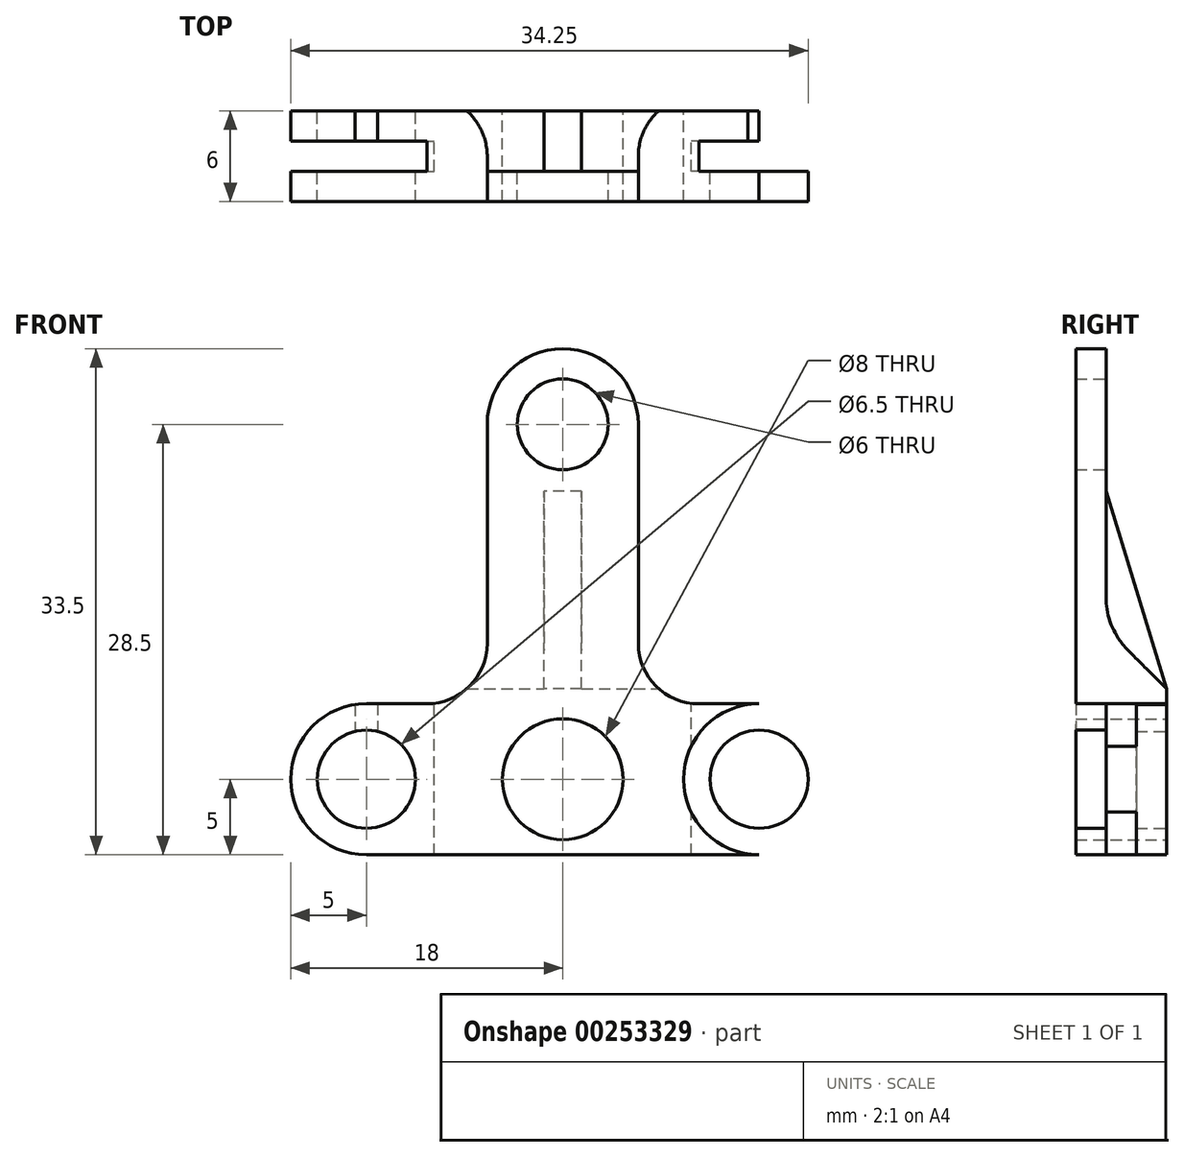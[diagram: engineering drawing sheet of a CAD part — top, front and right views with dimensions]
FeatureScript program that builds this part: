
annotation { "Feature Type Name" : "Feature", "Feature Type Description" : "" }
export const myFeature = defineFeature(function(context is Context, id is Id, definition is map)
    precondition{}
    {
        {
            var Q0;
            Q0=qCreatedBy(makeId("Front.planeOp"),FACE);
            var sketch = newSketch(context, id + "F0", { "sketchPlane" : qUnion([Q0])});
            skCircle(sketch, "E0", {"center": v(-13, 0) * mm, "radius": 3.25 * mm});
            skCircle(sketch, "E1", {"center": v(-13, 0) * mm, "radius": 5 * mm});
            skCircle(sketch, "E2", {"center": v(0, 0) * mm, "radius": 4 * mm});
            skCircle(sketch, "E3", {"center": v(0, 23.5) * mm, "radius": 3 * mm});
            skArc(sketch, "E4", {"start": v(5, 23.5) * mm, "mid": v(0, 28.5) * mm, "end": v(-5, 23.5) * mm});
            skCircle(sketch, "E5.MirrorC", {"center": v(13, 0) * mm, "radius": 5 * mm});
            skCircle(sketch, "E6.MirrorC", {"center": v(13, 0) * mm, "radius": 3.25 * mm});
            skLineSegment(sketch, "E7", {"start": v(-5, 23.5) * mm, "end": v(-5, 9) * mm});
            skLineSegment(sketch, "E8", {"start": v(-13, 5) * mm, "end": v(-9, 5) * mm});
            skArc(sketch, "E9", {"start": v(-9, 5) * mm, "mid": v(-6.17, 6.17) * mm, "end": v(-5, 9) * mm});
            skLineSegment(sketch, "E10.MirrorCS", {"start": v(5, 23.5) * mm, "end": v(5, 9) * mm});
            skArc(sketch, "E11.MirrorCS", {"start": v(9, 5) * mm, "mid": v(6.17, 6.17) * mm, "end": v(5, 9) * mm});
            skLineSegment(sketch, "E12.MirrorCS", {"start": v(13, 5) * mm, "end": v(9, 5) * mm});
            skLineSegment(sketch, "E13", {"start": v(-13, -5) * mm, "end": v(13, -5) * mm});
            skSolve(sketch);
        }
        {
            var Q0;
            Q0=makeQuery(id+"F0.imprint","IMPRINT",FACE,{"disambiguationData":[TD([[makeQuery(id+"F0.imprint","IMPRINT",EDGE,{"derivedFrom":sQuery(id+"F0.wireOp",EDGE,"E2")}),-1.0]])]});
            var Q1;
            Q1=makeQuery(id+"F0.imprint","IMPRINT",FACE,{"disambiguationData":[TD([[makeQuery(id+"F0.imprint","IMPRINT",EDGE,{"derivedFrom":sQuery(id+"F0.wireOp",EDGE,"E0")}),-1.0]])]});
            var Q2;
            Q2=makeQuery(id+"F0.imprint","IMPRINT",FACE,{"disambiguationData":[TD([[makeQuery(id+"F0.imprint","IMPRINT",EDGE,{"derivedFrom":sQuery(id+"F0.wireOp",EDGE,"E6.MirrorC")}),1.0]])]});
            extrude(context, id + "F1", {"entities" : qUnion([Q0, Q1, Q2]), "depth" : 6 * mm});
        }
        {
            var Q0;
            Q0=qCreatedBy(makeId("Right.planeOp"),FACE);
            var sketch = newSketch(context, id + "F2", { "sketchPlane" : qUnion([Q0])});
            skPoint(sketch, "E14", {"position": v(0, 6) * mm});
            skLineSegment(sketch, "E15", {"start": v(-6, 28.5) * mm, "end": v(-4, 28.5) * mm});
            skLineSegment(sketch, "E16", {"start": v(-6, 28.5) * mm, "end": v(-6, 6) * mm, "construction": true});
            skLineSegment(sketch, "E17", {"start": v(-6, 6) * mm, "end": v(0, 6) * mm, "construction": true});
            skLineSegment(sketch, "E18", {"start": v(-4, 28.5) * mm, "end": v(-4, 12.07) * mm});
            skLineSegment(sketch, "E19", {"start": v(0, 6) * mm, "end": v(-2.54, 8.54) * mm});
            skArc(sketch, "E20", {"start": v(-2.54, 8.54) * mm, "mid": v(-3.62, 10.16) * mm, "end": v(-4, 12.07) * mm});
            skLineSegment(sketch, "E21", {"start": v(-6, 28.5) * mm, "end": v(0, 28.5) * mm});
            skLineSegment(sketch, "E22", {"start": v(0, 28.5) * mm, "end": v(0, 6) * mm});
            skSolve(sketch);
        }
        {
            var Q0;
            Q0 = qSketchRegion(id + "F2", true);
            extrude(context, id + "F3", {"entities" : qUnion([Q0]), "operationType" : NewBodyOperationType.REMOVE, "endBound" : BoundingType.SYMMETRIC, "oppositeDirection" : true, "depth" : 25 * mm});
        }
        {
            var Q0;
            Q0=qCreatedBy(makeId("Right.planeOp"),FACE);
            var sketch = newSketch(context, id + "F4", { "sketchPlane" : qUnion([Q0])});
            skLineSegment(sketch, "E23", {"start": v(0, 6) * mm, "end": v(-2.54, 8.54) * mm});
            skArc(sketch, "E24", {"start": v(-2.54, 8.54) * mm, "mid": v(-3.62, 10.16) * mm, "end": v(-4, 12.07) * mm});
            skLineSegment(sketch, "E25", {"start": v(-4, 20.5) * mm, "end": v(-4, 12.07) * mm});
            skLineSegment(sketch, "E26", {"start": v(-4, 28.5) * mm, "end": v(-4, 26.5) * mm});
            skLineSegment(sketch, "E27", {"start": v(0, 6) * mm, "end": v(-4, 19.08) * mm});
            skSolve(sketch);
        }
        {
            var Q0;
            Q0 = qSketchRegion(id + "F4", true);
            extrude(context, id + "F5", {"entities" : qUnion([Q0]), "operationType" : NewBodyOperationType.ADD, "endBound" : BoundingType.SYMMETRIC, "depth" : 2.5 * mm});
        }
        {
            var Q0;
            Q0=makeQuery(id+"F1.opExtrude","SWEPT_FACE",FACE,{"disambiguationData":[OSD([sQuery(id+"F0.wireOp",EDGE,"E12.MirrorCS")])]});
            var sketch = newSketch(context, id + "F6", { "sketchPlane" : qUnion([Q0])});
            skLineSegment(sketch, "E28.bottom", {"start": v(18, -4) * mm, "end": v(8.5, -4) * mm});
            skLineSegment(sketch, "E28.top", {"start": v(18, -2) * mm, "end": v(8.5, -2) * mm});
            skLineSegment(sketch, "E28.left", {"start": v(18, -4) * mm, "end": v(18, -2) * mm});
            skLineSegment(sketch, "E28.right", {"start": v(8.5, -4) * mm, "end": v(8.5, -2) * mm});
            skPoint(sketch, "E29.0", {"position": v(18, -6) * mm});
            skLineSegment(sketch, "E30", {"start": v(18, -6) * mm, "end": v(18, 1.17) * mm, "construction": true});
            skLineSegment(sketch, "E31.MirrorCS", {"start": v(-18, -4) * mm, "end": v(-8.5, -4) * mm});
            skLineSegment(sketch, "E32.MirrorCS", {"start": v(-18, -2) * mm, "end": v(-8.5, -2) * mm});
            skLineSegment(sketch, "E33.MirrorCS", {"start": v(-8.5, -4) * mm, "end": v(-8.5, -2) * mm});
            skLineSegment(sketch, "E34.MirrorCS", {"start": v(-18, -6) * mm, "end": v(-18, 1.17) * mm, "construction": true});
            skLineSegment(sketch, "E35", {"start": v(-18, -4) * mm, "end": v(-18, -2) * mm});
            skSolve(sketch);
        }
        {
            var Q0;
            Q0 = qSketchRegion(id + "F6", true);
            extrude(context, id + "F7", {"entities" : qUnion([Q0]), "operationType" : NewBodyOperationType.REMOVE, "oppositeDirection" : true, "depth" : 25 * mm});
        }
        {
            var Q0;
            Q0=makeQuery(id+"F1.opExtrude","CAP_FACE",FACE,{"disambiguationData":[OSD([sQuery(id+"F0.wireOp",EDGE,"E0"),sQuery(id+"F0.wireOp",EDGE,"E1"),sQuery(id+"F0.wireOp",EDGE,"E2"),sQuery(id+"F0.wireOp",EDGE,"E3"),sQuery(id+"F0.wireOp",EDGE,"E4"),sQuery(id+"F0.wireOp",EDGE,"E5.MirrorC"),sQuery(id+"F0.wireOp",EDGE,"E6.MirrorC"),sQuery(id+"F0.wireOp",EDGE,"E7"),sQuery(id+"F0.wireOp",EDGE,"E8"),sQuery(id+"F0.wireOp",EDGE,"E9"),sQuery(id+"F0.wireOp",EDGE,"E10.MirrorCS"),sQuery(id+"F0.wireOp",EDGE,"E11.MirrorCS"),sQuery(id+"F0.wireOp",EDGE,"E12.MirrorCS"),sQuery(id+"F0.wireOp",EDGE,"E13")])],"isStart":true});
            var sketch = newSketch(context, id + "F8", { "sketchPlane" : qUnion([Q0])});
            skLineSegment(sketch, "E36.bottom", {"start": v(12.25, 6.82) * mm, "end": v(13.75, 6.82) * mm});
            skLineSegment(sketch, "E36.top", {"start": v(12.25, 1.07) * mm, "end": v(13.75, 1.07) * mm});
            skLineSegment(sketch, "E36.left", {"start": v(12.25, 6.82) * mm, "end": v(12.25, 1.07) * mm});
            skLineSegment(sketch, "E36.right", {"start": v(13.75, 6.82) * mm, "end": v(13.75, 1.07) * mm});
            skCircle(sketch, "E37.0", {"center": v(13, 0) * mm, "radius": 3.25 * mm});
            skCircle(sketch, "E38.MirrorC", {"center": v(-13, 0) * mm, "radius": 3.25 * mm});
            skLineSegment(sketch, "E39.MirrorCS", {"start": v(-13.75, 6.82) * mm, "end": v(-13.75, 1.07) * mm});
            skLineSegment(sketch, "E40.MirrorCS", {"start": v(-12.25, 1.07) * mm, "end": v(-13.75, 1.07) * mm});
            skLineSegment(sketch, "E41.MirrorCS", {"start": v(-12.25, 6.82) * mm, "end": v(-13.75, 6.82) * mm});
            skLineSegment(sketch, "E42.MirrorCS", {"start": v(-12.25, 6.82) * mm, "end": v(-12.25, 1.07) * mm});
            skSolve(sketch);
        }
        {
            var Q0;
            Q0 = qSketchRegion(id + "F8", true);
            var Q1;
            Q1=makeQuery(id+"F8.imprint","IMPRINT",FACE,{"disambiguationData":[TD([[makeQuery(id+"F8.imprint","IMPRINT",EDGE,{"derivedFrom":makeQuery(id+"F1.opExtrude","CAP_EDGE",EDGE,{"disambiguationData":[OSD([sQuery(id+"F0.wireOp",EDGE,"E6.MirrorC")])],"isStart":true})}),1.0]])]});
            extrude(context, id + "F9", {"entities" : qUnion([Q0, Q1]), "operationType" : NewBodyOperationType.REMOVE, "oppositeDirection" : true, "depth" : 2 * mm});
        }
    });
